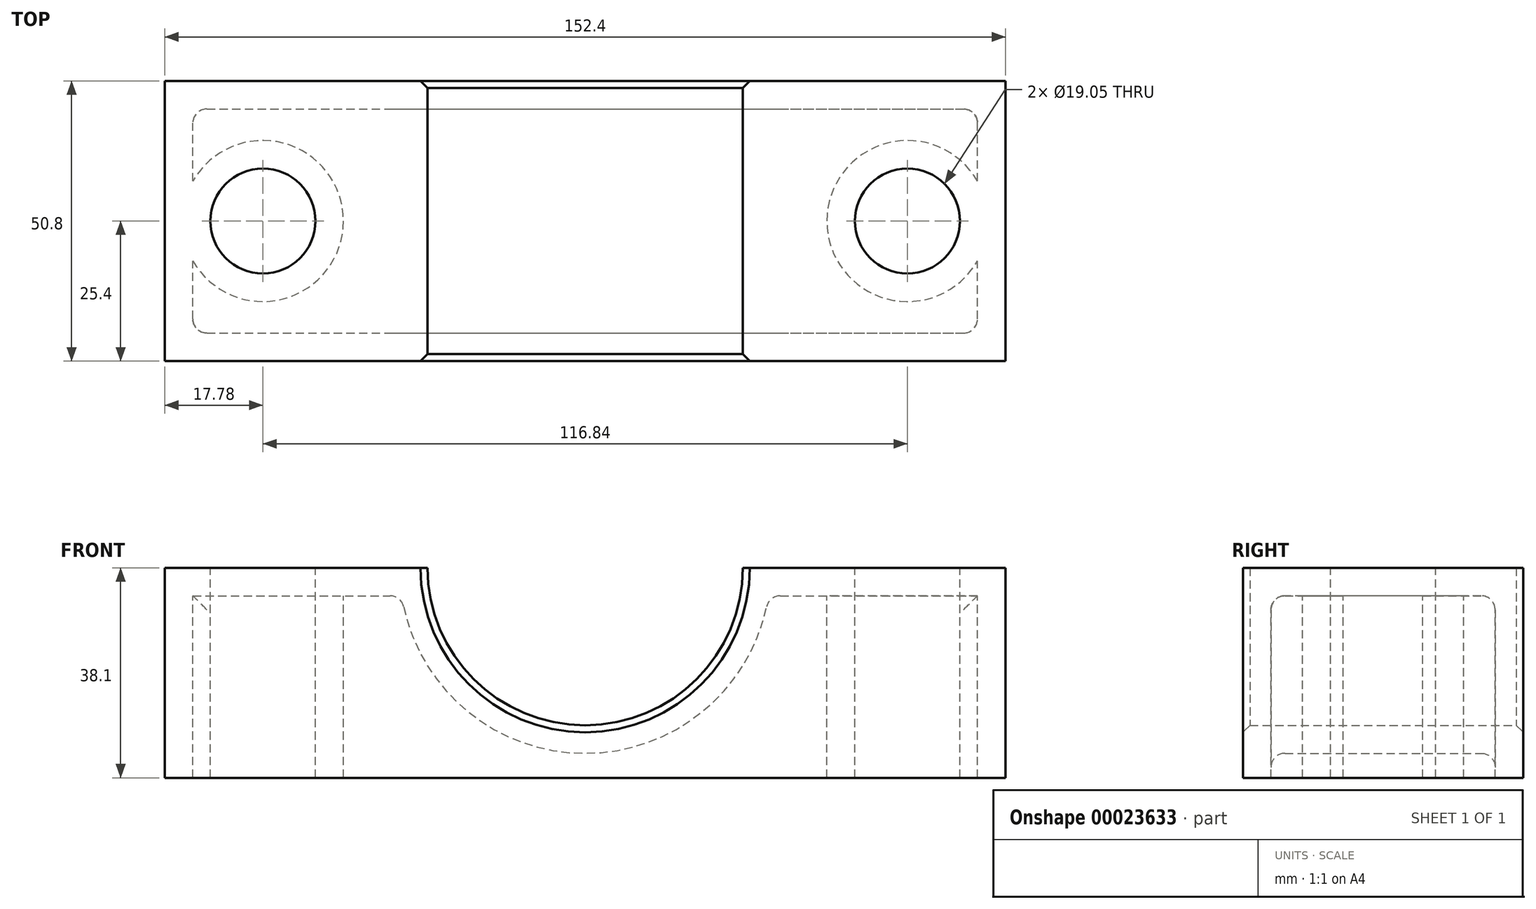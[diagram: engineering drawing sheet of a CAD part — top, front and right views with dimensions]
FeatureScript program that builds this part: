
annotation { "Feature Type Name" : "Feature", "Feature Type Description" : "" }
export const myFeature = defineFeature(function(context is Context, id is Id, definition is map)
    precondition{}
    {
        {
            var Q0;
            Q0=qCreatedBy(makeId("Front.planeOp"),FACE);
            var sketch = newSketch(context, id + "F0", { "sketchPlane" : qUnion([Q0])});
            skLineSegment(sketch, "E0", {"start": v(0, 38.1) * mm, "end": v(0, -62.73) * mm, "construction": true});
            skLineSegment(sketch, "E1.bottom", {"start": v(-76.2, 0) * mm, "end": v(76.2, 0) * mm});
            skLineSegment(sketch, "E1.top", {"start": v(-76.2, 38.1) * mm, "end": v(-28.58, 38.1) * mm});
            skLineSegment(sketch, "E1.left", {"start": v(-76.2, 0) * mm, "end": v(-76.2, 38.1) * mm});
            skLineSegment(sketch, "E1.right", {"start": v(76.2, 0) * mm, "end": v(76.2, 38.1) * mm});
            skArc(sketch, "E2", {"start": v(-28.57, 38.1) * mm, "mid": v(0, 9.52) * mm, "end": v(28.58, 38.1) * mm});
            skPoint(sketch, "E3.orphan", {"position": v(0, 65.58) * mm});
            skLineSegment(sketch, "E4.trimOffspring", {"start": v(28.58, 38.1) * mm, "end": v(76.2, 38.1) * mm});
            skSolve(sketch);
        }
        {
            var Q0;
            Q0 = qSketchRegion(id + "F0", true);
            extrude(context, id + "F1", {"entities" : qUnion([Q0]), "endBound" : BoundingType.SYMMETRIC, "depth" : 50.8 * mm});
        }
        {
            var Q0;
            Q0=makeQuery(id+"F1.opExtrude","SWEPT_FACE",FACE,{"disambiguationData":[OSD([sQuery(id+"F0.wireOp",EDGE,"E1.top")])]});
            var sketch = newSketch(context, id + "F2", { "sketchPlane" : qUnion([Q0])});
            skPoint(sketch, "E5", {"position": v(-58.42, 0) * mm});
            skPoint(sketch, "E6", {"position": v(58.42, 0) * mm});
            skLineSegment(sketch, "E7", {"start": v(0, -57.79) * mm, "end": v(0, 57.4) * mm, "construction": true});
            skSolve(sketch);
        }
        {
            var Q0;
            Q0=sQuery(id+"F2.wireOp",VERTEX,"E5");
            var Q1;
            Q1=sQuery(id+"F2.wireOp",VERTEX,"E6");
            var Q2;
            Q2=makeQuery(id+"F1.opExtrude","SWEPT_BODY",BODY,{"disambiguationData":[OSD([sQuery(id+"F0.wireOp",EDGE,"E1.bottom"),sQuery(id+"F0.wireOp",EDGE,"E1.top"),sQuery(id+"F0.wireOp",EDGE,"E1.left"),sQuery(id+"F0.wireOp",EDGE,"E1.right"),sQuery(id+"F0.wireOp",EDGE,"E2"),sQuery(id+"F0.wireOp",EDGE,"E4.trimOffspring")])]});
            hole(context, id + "F3", {"style" : HoleStyle.SIMPLE, "holeDiameter" : 19.05 * mm, "endStyle" : HoleEndStyle.THROUGH, "locations" : qUnion([Q0, Q1]), "scope" : qUnion([Q2])});
        }
        {
            var Q0;
            Q0=makeQuery(id+"F1.opExtrude","CAP_EDGE",EDGE,{"disambiguationData":[OSD([sQuery(id+"F0.wireOp",EDGE,"E2")])],"isStart":true});
            var Q1;
            Q1=makeQuery(id+"F1.opExtrude","CAP_EDGE",EDGE,{"disambiguationData":[OSD([sQuery(id+"F0.wireOp",EDGE,"E2")])],"isStart":false});
            chamfer(context, id + "F4", {"entities" : qUnion([Q0, Q1]), "width" : 1.27 * mm, "tangentPropagation" : true});
        }
        {
            var Q0;
            Q0=makeQuery(id+"F1.opExtrude","SWEPT_FACE",FACE,{"disambiguationData":[OSD([sQuery(id+"F0.wireOp",EDGE,"E1.bottom")])]});
            shell(context, id + "F5", {"entities" : qUnion([Q0]), "thickness" : 5.08 * mm});
        }
        {
            var Q0;
            Q0=makeQuery(id+"F5.opShell","TWEAK_EDGE",EDGE,{"disambiguationData":[OD(1.0)],"derivedFrom":[makeQuery(id+"F1.opExtrude","SWEPT_FACE",FACE,{"disambiguationData":[OSD([sQuery(id+"F0.wireOp",EDGE,"E1.left")])]}),makeQuery(id+"F3.hole-0.boolean.opBoolean","COPY",FACE,{"derivedFrom":makeQuery(id+"F3.hole-0.opRevolve","SWEPT_FACE",FACE,{"disambiguationData":[OSD([sQuery(id+"F3.hole-0.sketch.wireOp",EDGE,"core_line_2")])]})})]});
            var Q1;
            {var subQ0=sQuery(id+"F0.wireOp",EDGE,"E1.left");Q1=makeQuery(id+"F5.opShell","OFFSET_EDGE",EDGE,{"disambiguationData":[OSD([subQ0]),TDD([makeQuery(id+"F1.opExtrude","CAP_EDGE",EDGE,{"disambiguationData":[OSD([subQ0])],"isStart":false})])]});}
            var Q2;
            Q2=makeQuery(id+"F5.opShell","OFFSET_EDGE",EDGE,{"disambiguationData":[OSD([sQuery(id+"F0.wireOp",EDGE,"E1.top"),sQuery(id+"F0.wireOp",EDGE,"E2")])]});
            var Q3;
            {var subQ0=sQuery(id+"F0.wireOp",EDGE,"E1.left");Q3=makeQuery(id+"F5.opShell","OFFSET_EDGE",EDGE,{"disambiguationData":[OSD([subQ0]),TDD([makeQuery(id+"F1.opExtrude","CAP_EDGE",EDGE,{"disambiguationData":[OSD([subQ0])],"isStart":true})])]});}
            var Q4;
            Q4=makeQuery(id+"F5.opShell","TWEAK_EDGE",EDGE,{"disambiguationData":[OD(0.0)],"derivedFrom":[makeQuery(id+"F1.opExtrude","SWEPT_FACE",FACE,{"disambiguationData":[OSD([sQuery(id+"F0.wireOp",EDGE,"E1.left")])]}),makeQuery(id+"F3.hole-0.boolean.opBoolean","COPY",FACE,{"derivedFrom":makeQuery(id+"F3.hole-0.opRevolve","SWEPT_FACE",FACE,{"disambiguationData":[OSD([sQuery(id+"F3.hole-0.sketch.wireOp",EDGE,"core_line_2")])]})})]});
            var Q5;
            Q5=makeQuery(id+"F5.opShell","OFFSET_EDGE",EDGE,{"disambiguationData":[OSD([sQuery(id+"F0.wireOp",EDGE,"E2"),sQuery(id+"F0.wireOp",EDGE,"E4.trimOffspring")])]});
            var Q6;
            Q6=makeQuery(id+"F5.opShell","TWEAK_EDGE",EDGE,{"disambiguationData":[OD(0.0)],"derivedFrom":[makeQuery(id+"F1.opExtrude","SWEPT_FACE",FACE,{"disambiguationData":[OSD([sQuery(id+"F0.wireOp",EDGE,"E1.right")])]}),makeQuery(id+"F3.hole-1.boolean.opBoolean","COPY",FACE,{"derivedFrom":makeQuery(id+"F3.hole-1.opRevolve","SWEPT_FACE",FACE,{"disambiguationData":[OSD([sQuery(id+"F3.hole-1.sketch.wireOp",EDGE,"core_line_2")])]})})]});
            var Q7;
            {var subQ0=sQuery(id+"F0.wireOp",EDGE,"E1.right");Q7=makeQuery(id+"F5.opShell","OFFSET_EDGE",EDGE,{"disambiguationData":[OSD([subQ0]),TDD([makeQuery(id+"F1.opExtrude","CAP_EDGE",EDGE,{"disambiguationData":[OSD([subQ0])],"isStart":true})])]});}
            var Q8;
            Q8=makeQuery(id+"F5.opShell","TWEAK_EDGE",EDGE,{"disambiguationData":[OD(1.0)],"derivedFrom":[makeQuery(id+"F1.opExtrude","SWEPT_FACE",FACE,{"disambiguationData":[OSD([sQuery(id+"F0.wireOp",EDGE,"E1.right")])]}),makeQuery(id+"F3.hole-1.boolean.opBoolean","COPY",FACE,{"derivedFrom":makeQuery(id+"F3.hole-1.opRevolve","SWEPT_FACE",FACE,{"disambiguationData":[OSD([sQuery(id+"F3.hole-1.sketch.wireOp",EDGE,"core_line_2")])]})})]});
            var Q9;
            {var subQ0=sQuery(id+"F0.wireOp",EDGE,"E1.right");Q9=makeQuery(id+"F5.opShell","OFFSET_EDGE",EDGE,{"disambiguationData":[OSD([subQ0]),TDD([makeQuery(id+"F1.opExtrude","CAP_EDGE",EDGE,{"disambiguationData":[OSD([subQ0])],"isStart":false})])]});}
            var Q10;
            Q10=makeQuery(id+"F5.opShell","OFFSET_EDGE",EDGE,{"disambiguationData":[OSD([sQuery(id+"F3.hole-1.sketch.wireOp",EDGE,"core_line_2"),sQuery(id+"F3.hole-1.sketch.wireOp",EDGE,"core_line_3")])]});
            var Q11;
            Q11=makeQuery(id+"F5.opShell","OFFSET_EDGE",EDGE,{"disambiguationData":[OSD([sQuery(id+"F3.hole-0.sketch.wireOp",EDGE,"core_line_2"),sQuery(id+"F3.hole-0.sketch.wireOp",EDGE,"core_line_3")])]});
            var Q12;
            {var subQ0=sQuery(id+"F0.wireOp",EDGE,"E2");Q12=makeQuery(id+"F5.opShell","TWEAK_EDGE",EDGE,{"derivedFrom":[makeQuery(id+"F1.opExtrude","CAP_FACE",FACE,{"disambiguationData":[OSD([sQuery(id+"F0.wireOp",EDGE,"E1.bottom"),sQuery(id+"F0.wireOp",EDGE,"E1.top"),sQuery(id+"F0.wireOp",EDGE,"E1.left"),sQuery(id+"F0.wireOp",EDGE,"E1.right"),subQ0,sQuery(id+"F0.wireOp",EDGE,"E4.trimOffspring")])],"isStart":false}),makeQuery(id+"F1.opExtrude","SWEPT_FACE",FACE,{"disambiguationData":[OSD([subQ0])]})]});}
            var Q13;
            {var subQ0=sQuery(id+"F0.wireOp",EDGE,"E2");Q13=makeQuery(id+"F5.opShell","TWEAK_EDGE",EDGE,{"derivedFrom":[makeQuery(id+"F1.opExtrude","CAP_FACE",FACE,{"disambiguationData":[OSD([sQuery(id+"F0.wireOp",EDGE,"E1.bottom"),sQuery(id+"F0.wireOp",EDGE,"E1.top"),sQuery(id+"F0.wireOp",EDGE,"E1.left"),sQuery(id+"F0.wireOp",EDGE,"E1.right"),subQ0,sQuery(id+"F0.wireOp",EDGE,"E4.trimOffspring")])],"isStart":true}),makeQuery(id+"F1.opExtrude","SWEPT_FACE",FACE,{"disambiguationData":[OSD([subQ0])]})]});}
            var Q14;
            {var subQ0=sQuery(id+"F0.wireOp",EDGE,"E4.trimOffspring");Q14=makeQuery(id+"F5.opShell","OFFSET_EDGE",EDGE,{"disambiguationData":[OSD([subQ0]),TDD([makeQuery(id+"F1.opExtrude","CAP_EDGE",EDGE,{"disambiguationData":[OSD([subQ0])],"isStart":false})])]});}
            var Q15;
            {var subQ0=sQuery(id+"F0.wireOp",EDGE,"E4.trimOffspring");Q15=makeQuery(id+"F5.opShell","OFFSET_EDGE",EDGE,{"disambiguationData":[OSD([subQ0]),TDD([makeQuery(id+"F1.opExtrude","CAP_EDGE",EDGE,{"disambiguationData":[OSD([subQ0])],"isStart":true})])]});}
            var Q16;
            {var subQ0=sQuery(id+"F0.wireOp",EDGE,"E1.top");Q16=makeQuery(id+"F5.opShell","OFFSET_EDGE",EDGE,{"disambiguationData":[OSD([subQ0]),TDD([makeQuery(id+"F1.opExtrude","CAP_EDGE",EDGE,{"disambiguationData":[OSD([subQ0])],"isStart":true})])]});}
            var Q17;
            {var subQ0=sQuery(id+"F0.wireOp",EDGE,"E1.top");Q17=makeQuery(id+"F5.opShell","OFFSET_EDGE",EDGE,{"disambiguationData":[OSD([subQ0]),TDD([makeQuery(id+"F1.opExtrude","CAP_EDGE",EDGE,{"disambiguationData":[OSD([subQ0])],"isStart":false})])]});}
            fillet(context, id + "F6", {"entities" : qUnion([Q0, Q1, Q2, Q3, Q4, Q5, Q6, Q7, Q8, Q9, Q10, Q11, Q12, Q13, Q14, Q15, Q16, Q17]), "radius" : 2.54 * mm, "tangentPropagation" : true, "allowEdgeOverflow" : false});
        }
    });
